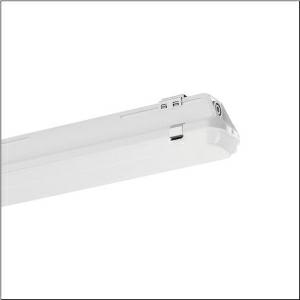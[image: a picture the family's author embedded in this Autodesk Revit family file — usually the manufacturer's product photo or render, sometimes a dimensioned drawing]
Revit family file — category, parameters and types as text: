
# Revit family: monsun_21_emergency_51fb207p467c3g
name_source: partatom
category: Lighting Fixtures
units: mm (PartAtom-declared; Revit-internal decimal feet)

## family parameters
Cut with Voids When Loaded = No
Host = Face
Light Source = No
Part Type = Normal
Room Calculation Point = No
Round Connector Dimension = Use Diameter
Shared = No

## types (1)
- --- (1 x LED, 820 lm, 7.1 W, 4000K)
    Apparent Load = 7 VA
    CIE Flux Codes = 45 75 93 94 100
    Color Rendering = 80
    Color Temperature = 4000K
    Default Elevation = 1800 mm
    Description = Monsun 21 emergency, damp-proof luminaire, chain hanger, primary optical cover: enclosure, of PC, light emission: direct distribution, primary light characteristic: symmetric, installation type: suspended mounting, surface-mounted, horizontal mounting, vertical mounting, LED, rated luminous flux: 5.460lm, luminous efficacy: 160lm/W, light colour: 840, colour temperature: 4000K, control gear: ON/OFF, with terminal, 4-pole, max. 2.5mm², mains connection: 220..240V, AC, 50/60Hz, rated input power: 38W, control gear: single battery element, battery: LiFePO4, 9Ah, housing, of glass-fibre reinforced polyester, uncoated, bright grey, incl. chain hanger, length: 1.590mm, width: 90mm, height: 88mm, clip for enclosure, of stainless steel (V2A), ceiling mounting element, of stainless steel (V2A), chain hanger, of stainless steel (V2A), protection rating (complete): IP66, insulation class (complete): insulation class I (protective earthing), certification: CE, UKCA, protection symbol: D, impact resistance: IK08, permissible operating ambient temperature: +5..+25°C, standard: EN 50419, EN 60598-2-1, EN 60598-2-22, corresponds to IFS (International Featured Standards) requirements for safety and quality in the food industry, for indoor or canopied outdoor use, no direct snow, no direct sun, no direct rain, LABS conformity tested according to VDMA 24364:2018-05, contact your sales advisor before using the luminaires in applications with unclear chemical exposure, large temperature fluctuations or condensation-forming humidity, packaging unit: 1 piece
    Height = 89 mm
    Lamp = 1 x LED
    Lamp Light Flux = 820 lm
    Lamp Power = 7.1 W
    Lamp count = 1
    Length = 1590 mm
    Luminous efficacy = 115 lm/W
    Manufacturer = Siteco
    ModVariant = No
    Model = 51FB207P467C3G
    Mounting Place = Ceiling
    Mounting Type = Surface mounted
    Number of Poles = 1
    OnlyDefault = Yes
    Power Factor = 1
    Product Name = Monsun 21 emergency
    Product group = damp-proof luminaire
    ProductGroupID = 300
    Protection Class = Protection class I
    Protection Degree = IP 66
    RLX_Detail_Level = 1
    RLX_Emergency_Light_Flux = 0 lm
    RLX_Emergency_Type = 0
    RLX_Emergency_Type_DB = No
    RlxData = <blob elided: 88969 chars, md5=9d8581a1>
    Socket = socket
    Standby Power = 0 W
    System Light Flux = 820 lm
    System Power = 7 W
    Type Comments = : emergency light operation: 3 h
    Type Image = l_1319656.jpg
    URL = http://relux.com
    VarID = @adj_049313
    Voltage = 0 V
    Weight = 0.00 kg
    Width = 90 mm

## geometry (parser evidence)
native form markers: Blend x4, Sweep x13
no freeform markers — native parametric forms only
